# Revit family: НЕВАТОМ_Решетка для клапана KD_20220407
name_source: partatom
category: Воздухораспределители
revit_build: Autodesk Revit 2017 (Build: 20170118_1100(x64)
units: mm (PartAtom-declared; Revit-internal decimal feet)

## family parameters
Всегда вертикально = Нет
На основе рабочей плоскости = Нет
Общий = Нет
При загрузке вырезать с полостями = Нет
Размер круглого соединителя = Использовать диаметр
Тип детали = Нормальный
Точка расчета площади = Нет

## types (27) — shared parameters
ADSK_Единица измерения = шт
ADSK_Завод-изготовитель = NEVATOM
ADSK_Материал наименование = Оцинкованная сталь
ADSK_Наименование = РЕШЕТКА
ADSK_Потеря давления воздуха = 0.0 Па
ADSK_Размер_Ширина = 30 мм
ADSK_Расход воздуха = 0.0 л/с
L = 30 мм
Nevatom_URL = https://t.me
t = 2 мм
Материал = Материал корпуса

## per-type parameters (varying)
| type | A | A-60 | A1 | ADSK_Марка | ADSK_Масса | ADSK_Масса_Текст | ADSK_Размер_Высота | ADSK_Размер_Длина | B | B1 | C | N |
| 200x200 | 200 мм | 230 мм | 290 мм | KD-200Х200-30-ОЦ.-1,0-RAL6029 | 0.05 | 0,050 кг | 300 мм | 290 мм | 200 мм | 300 мм | 35 мм | 6 |
| 250x250 | 250 мм | 280 мм | 340 мм | KD-250Х250-30-ОЦ.-1,0-RAL6029 | 0.061 | 0,061 кг | 350 мм | 340 мм | 250 мм | 350 мм | 35 мм | 7 |
| 300x300 | 300 мм | 330 мм | 390 мм | KD-300Х300-30-ОЦ.-1,0-RAL6029 | 0.072 | 0,072 кг | 400 мм | 390 мм | 300 мм | 400 мм | 25 мм | 9 |
| 350x350 | 350 мм | 380 мм | 440 мм | KD-350Х350-30-ОЦ.-1,0-RAL6029 | 0.083 | 0,083 кг | 450 мм | 440 мм | 350 мм | 450 мм | 30 мм | 10 |
| 400x400 | 400 мм | 430 мм | 490 мм | KD-400Х400-30-ОЦ.-1,0-RAL6029 | 0.094 | 0,094 кг | 500 мм | 490 мм | 400 мм | 500 мм | 35 мм | 11 |
| 450x450 | 450 мм | 480 мм | 540 мм | KD-450Х450-30-ОЦ.-1,0-RAL6029 | 0.105 | 0,105 кг | 550 мм | 540 мм | 450 мм | 550 мм | 40 мм | 12 |
| 500x500 | 500 мм | 530 мм | 590 мм | KD-500Х500-30-ОЦ.-1,0-RAL6029 | 0.116 | 0,116 кг | 600 мм | 590 мм | 500 мм | 600 мм | 25 мм | 14 |
| 550x550 | 550 мм | 580 мм | 640 мм | KD-550Х550-30-ОЦ.-1,0-RAL6029 | 0.126 | 0,126 кг | 650 мм | 640 мм | 550 мм | 650 мм | 30 мм | 15 |
| 600x600 | 600 мм | 630 мм | 690 мм | KD-600Х600-30-ОЦ.-1,0-RAL6029 | 0.137 | 0,137 кг | 700 мм | 690 мм | 600 мм | 700 мм | 35 мм | 16 |
| 650x650 | 650 мм | 680 мм | 740 мм | KD-650Х650-30-ОЦ.-1,0-RAL6029 | 0.148 | 0,148 кг | 750 мм | 740 мм | 650 мм | 750 мм | 40 мм | 17 |
| 700x700 | 700 мм | 730 мм | 790 мм | KD-700Х700-30-ОЦ.-1,0-RAL6029 | 0.159 | 0,159 кг | 800 мм | 790 мм | 700 мм | 800 мм | 45 мм | 18 |
| 750x750 | 750 мм | 780 мм | 840 мм | KD-750Х750-30-ОЦ.-1,0-RAL6029 | 0.17 | 0,170 кг | 850 мм | 840 мм | 750 мм | 850 мм | 30 мм | 20 |
| 800x800 | 800 мм | 830 мм | 890 мм | KD-800Х800-30-ОЦ.-1,0-RAL6029 | 0.181 | 0,181 кг | 900 мм | 890 мм | 800 мм | 900 мм | 35 мм | 21 |
| 850x850 | 850 мм | 880 мм | 940 мм | KD-850Х850-30-ОЦ.-1,0-RAL6029 | 0.192 | 0,192 кг | 950 мм | 940 мм | 850 мм | 950 мм | 40 мм | 22 |
| 900x900 | 900 мм | 930 мм | 990 мм | KD-900Х900-30-ОЦ.-1,0-RAL6029 | 0.203 | 0,203 кг | 1000 мм | 990 мм | 900 мм | 1000 мм | 45 мм | 23 |
| 950x950 | 950 мм | 980 мм | 1040 мм | KD-950Х950-30-ОЦ.-1,0-RAL6029 | 0.214 | 0,214 кг | 1050 мм | 1040 мм | 950 мм | 1050 мм | 30 мм | 25 |
| 1000x1000 | 1000 мм | 1030 мм | 1090 мм | KD-1000Х1000-30-ОЦ.-1,0-RAL6029 | 0.225 | 0,225 кг | 1100 мм | 1090 мм | 1000 мм | 1100 мм | 35 мм | 26 |
| 1050x1050 | 1050 мм | 1080 мм | 1140 мм | KD-1050Х1050-30-ОЦ.-1,0-RAL6029 | 0.11 | 0,110 кг | 1150 мм | 1140 мм | 1050 мм | 1150 мм | 40 мм | 27 |
| 1100x1100 | 1100 мм | 1130 мм | 1190 мм | KD-1100Х1100-30-ОЦ.-1,0-RAL6029 | 0.116 | 0,116 кг | 1200 мм | 1190 мм | 1100 мм | 1200 мм | 45 мм | 28 |
| 1150x1150 | 1150 мм | 1180 мм | 1240 мм | KD-1150Х1150-30-ОЦ.-1,0-RAL6029 | 0.121 | 0,121 кг | 1250 мм | 1240 мм | 1150 мм | 1250 мм | 30 мм | 30 |
| 1200x1200 | 1200 мм | 1230 мм | 1290 мм | KD-1200Х1200-30-ОЦ.-1,0-RAL6029 | 0.126 | 0,126 кг | 1300 мм | 1290 мм | 1200 мм | 1300 мм | 35 мм | 31 |
| 1250x1250 | 1250 мм | 1280 мм | 1340 мм | KD-1250Х1250-30-ОЦ.-1,0-RAL6029 | 0.132 | 0,132 кг | 1350 мм | 1340 мм | 1250 мм | 1350 мм | 35 мм | 32 |
| 1300x1300 | 1300 мм | 1330 мм | 1390 мм | KD-1300Х1300-30-ОЦ.-1,0-RAL6029 | 0.137 | 0,137 кг | 1400 мм | 1390 мм | 1300 мм | 1400 мм | 45 мм | 33 |
| 1350x1350 | 1350 мм | 1380 мм | 1440 мм | KD-1350Х1350-30-ОЦ.-1,0-RAL6029 | 0.143 | 0,143 кг | 1450 мм | 1440 мм | 1350 мм | 1450 мм | 30 мм | 35 |
| 1400x1400 | 1400 мм | 1430 мм | 1490 мм | KD-1400Х1400-30-ОЦ.-1,0-RAL6029 | 0.148 | 0,148 кг | 1500 мм | 1490 мм | 1400 мм | 1500 мм | 35 мм | 36 |
| 1450x1450 | 1450 мм | 1480 мм | 1540 мм | KD-1450Х1450-30-ОЦ.-1,0-RAL6029 | 0.154 | 0,154 кг | 1550 мм | 1540 мм | 1450 мм | 1550 мм | 40 мм | 37 |
| 1500x1500 | 1500 мм | 1530 мм | 1590 мм | KD-1500Х1500-30-ОЦ.-1,0-RAL6029 | 0.159 | 0,159 кг | 1600 мм | 1590 мм | 1500 мм | 1600 мм | 45 мм | 38 |
